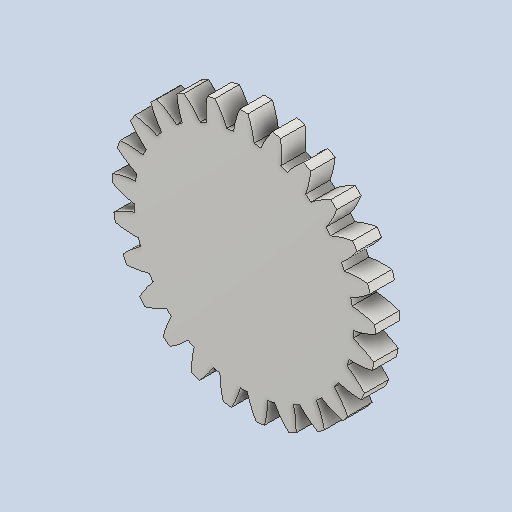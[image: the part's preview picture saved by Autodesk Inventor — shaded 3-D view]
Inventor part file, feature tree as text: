
AUTODESK INVENTOR PART (.ipt)
format: ipt  version: 2024 (Build 280153000, 153)  size: 244,736 bytes
history: native  units: mm (DEFAULTED — no unit token found)
features: plane x3, other x3, extrude x1, sketch x1
ambient origin geometry x8: Origin, YZ Plane, XZ Plane, XY Plane, X Axis, Y Axis, Z Axis, Center Point
bodies: Solid1 (feature_tree)
feature tree (8):
  extrude  "Extrusion1"  Depth=5.0mm TaperAngle=0.0deg
  plane  "Work Plane2"
  plane  "Work Plane8"
  plane  "Work Plane9"
  other  "Spur Gear"
  sketch  "Sketch1"  dims[d0=54.0mm d1=5.0mm d2=0.0mm d3=50.0mm d4=10.0mm d5=0.0mm d16=100.0mm d17=0.0mm d34=1.256637mm d39=0.0mm d41=0.0mm d43=100.0mm d46=100.0mm d47=0.0mm d48=0.0mm]
  other  "Srf1"
  other  "Pitch Diameter"
